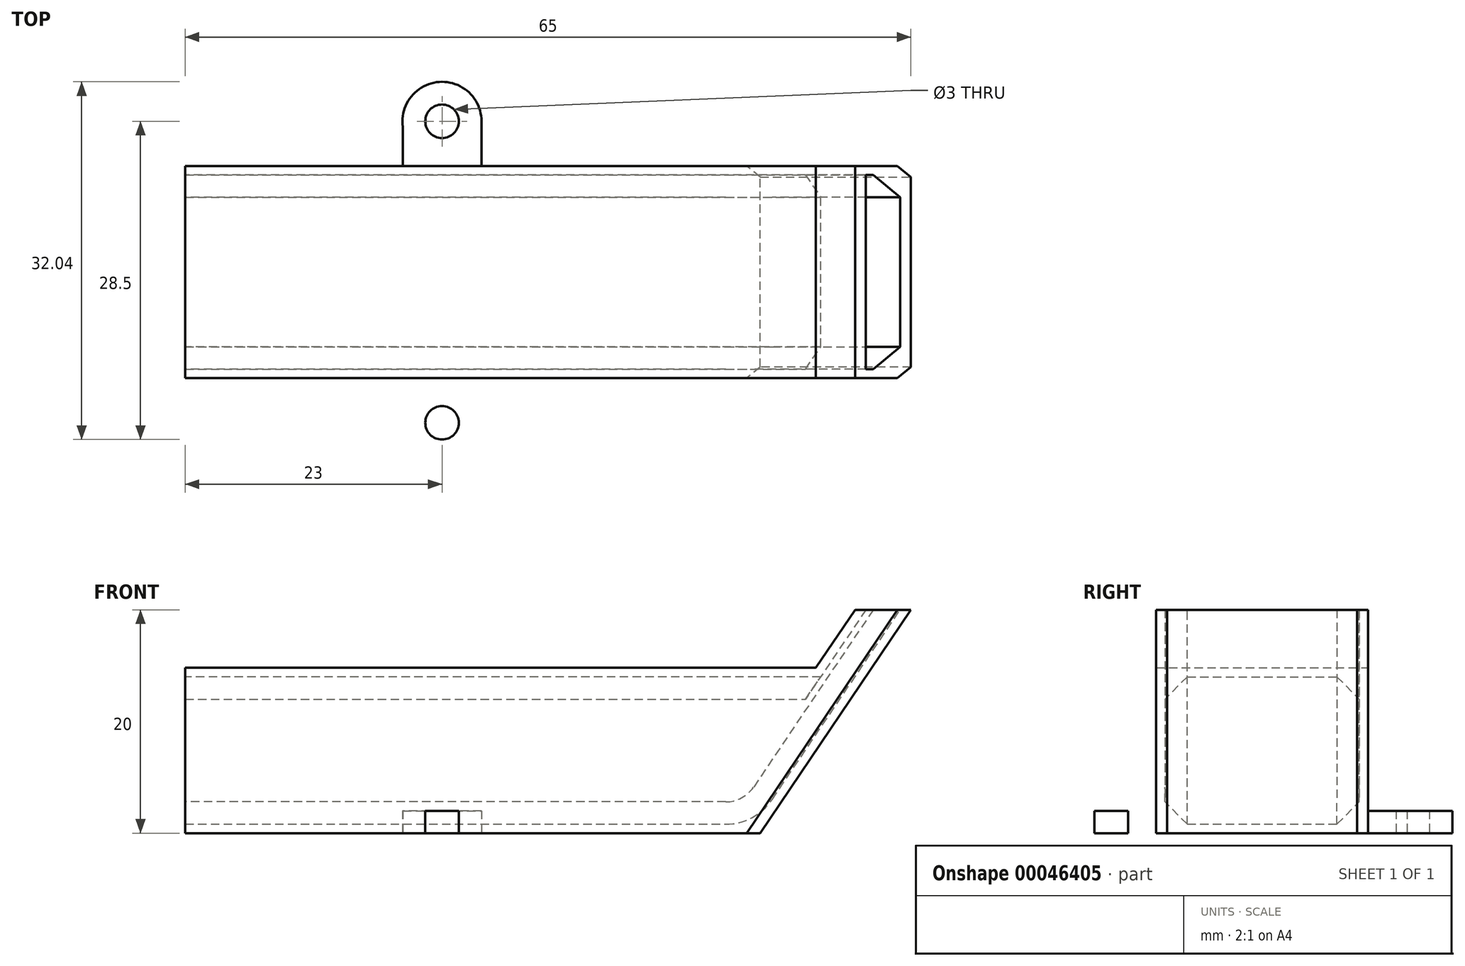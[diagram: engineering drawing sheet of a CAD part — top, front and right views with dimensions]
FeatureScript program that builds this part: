
annotation { "Feature Type Name" : "Feature", "Feature Type Description" : "" }
export const myFeature = defineFeature(function(context is Context, id is Id, definition is map)
    precondition{}
    {
        {
            var Q0;
            Q0=qCreatedBy(makeId("Top.planeOp"),FACE);
            var sketch = newSketch(context, id + "F0", { "sketchPlane" : qUnion([Q0])});
            skPoint(sketch, "E0.middle", {"position": v(0, 0) * mm});
            skLineSegment(sketch, "E1.MirrorCS", {"start": v(-24, -9.5) * mm, "end": v(-4.5, -9.5) * mm});
            skCircle(sketch, "E2.MirrorC", {"center": v(-1, -13.5) * mm, "radius": 1.5 * mm});
            skLineSegment(sketch, "E3.MirrorCS", {"start": v(-4.5, -13) * mm, "end": v(-4.5, -9.5) * mm});
            skLineSegment(sketch, "E4.MirrorCS", {"start": v(2.54, -13.5) * mm, "end": v(2.54, -9.5) * mm});
            skArc(sketch, "E5.MirrorCS", {"start": v(-4.5, -13) * mm, "mid": v(-1.25, -17.03) * mm, "end": v(2.54, -13.5) * mm});
            skLineSegment(sketch, "E6.MirrorCS", {"start": v(27.5, -9.5) * mm, "end": v(2.5, -9.5) * mm});
            skLineSegment(sketch, "E7", {"start": v(-4.5, -9.5) * mm, "end": v(2.54, -9.5) * mm});
            skLineSegment(sketch, "E8", {"start": v(27.5, -9.5) * mm, "end": v(27.5, 0) * mm});
            skLineSegment(sketch, "E9", {"start": v(-24, -9.5) * mm, "end": v(-24, 0) * mm});
            skLineSegment(sketch, "E10.MirrorCS", {"start": v(2.54, 13.5) * mm, "end": v(2.54, 9.5) * mm});
            skLineSegment(sketch, "E11.MirrorCS", {"start": v(-24, 9.5) * mm, "end": v(-24, 0) * mm});
            skLineSegment(sketch, "E12.MirrorCS", {"start": v(-4.5, 13) * mm, "end": v(-4.5, 9.5) * mm});
            skCircle(sketch, "E13.MirrorC", {"center": v(-1, 13.5) * mm, "radius": 1.5 * mm});
            skArc(sketch, "E14.MirrorCS", {"start": v(-4.5, 13) * mm, "mid": v(-1.25, 17.03) * mm, "end": v(2.54, 13.5) * mm});
            skLineSegment(sketch, "E15.MirrorCS", {"start": v(27.5, 9.5) * mm, "end": v(27.5, 0) * mm});
            skLineSegment(sketch, "E16.MirrorCS", {"start": v(-24, 9.5) * mm, "end": v(-4.5, 9.5) * mm});
            skLineSegment(sketch, "E17.MirrorCS", {"start": v(27.5, 9.5) * mm, "end": v(2.5, 9.5) * mm});
            skLineSegment(sketch, "E18.MirrorCS", {"start": v(-4.5, 9.5) * mm, "end": v(2.54, 9.5) * mm});
            skSolve(sketch);
        }
        {
            var Q0;
            Q0=qCreatedBy(makeId("Front.planeOp"),FACE);
            var sketch = newSketch(context, id + "F1", { "sketchPlane" : qUnion([Q0])});
            skLineSegment(sketch, "E19", {"start": v(27.5, 0) * mm, "end": v(-24, 0) * mm});
            skLineSegment(sketch, "E20", {"start": v(27.5, 0) * mm, "end": v(41, 20) * mm});
            skLineSegment(sketch, "E21", {"start": v(41, 20) * mm, "end": v(36, 20) * mm});
            skLineSegment(sketch, "E22", {"start": v(36, 20) * mm, "end": v(32.5, 14.8) * mm});
            skLineSegment(sketch, "E23", {"start": v(32.49, 14.8) * mm, "end": v(-24, 14.8) * mm});
            skLineSegment(sketch, "E24", {"start": v(-24, 14.8) * mm, "end": v(-24, 0) * mm});
            skSolve(sketch);
        }
        {
            var Q0;
            Q0=makeQuery(id+"F1.imprint","IMPRINT",FACE,{"disambiguationData":[TD([[makeQuery(id+"F1.imprint","IMPRINT",EDGE,{"derivedFrom":sQuery(id+"F1.wireOp",EDGE,"E19")}),-1.0]])]});
            extrude(context, id + "F2", {"entities" : qUnion([Q0]), "depth" : 19 * mm, "offsetDistance" : 25 * mm, "symmetric" : true});
        }
        {
            var Q0;
            Q0=makeQuery(id+"F2.opExtrude","SWEPT_FACE",FACE,{"disambiguationData":[OSD([sQuery(id+"F1.wireOp",EDGE,"E24")])]});
            var Q1;
            Q1=makeQuery(id+"F2.opExtrude","SWEPT_FACE",FACE,{"disambiguationData":[OSD([sQuery(id+"F1.wireOp",EDGE,"E21")])]});
            shell(context, id + "F3", {"entities" : qUnion([Q0, Q1]), "thickness" : 0.8 * mm});
        }
        {
            var Q0;
            Q0=makeQuery(id+"F3.opShell","OFFSET_EDGE",EDGE,{"disambiguationData":[OSD([sQuery(id+"F1.wireOp",EDGE,"E19"),sQuery(id+"F1.wireOp",EDGE,"E20")])]});
            fillet(context, id + "F4", {"entities" : qUnion([Q0]), "tangentPropagation" : true, "radius" : 5 * mm, "defaultsChanged" : true, "vertexSettings" : [], "allowEdgeOverflow" : false});
        }
        {
            var Q0;
            {var subQ0=sQuery(id+"F1.wireOp",EDGE,"E23");Q0=makeQuery(id+"F3.opShell","OFFSET_EDGE",EDGE,{"disambiguationData":[OSD([subQ0]),TDD([makeQuery(id+"F2.opExtrude","CAP_EDGE",EDGE,{"disambiguationData":[OSD([subQ0])],"isStart":false})])]});}
            var Q1;
            {var subQ0=sQuery(id+"F1.wireOp",EDGE,"E23");Q1=makeQuery(id+"F3.opShell","OFFSET_EDGE",EDGE,{"disambiguationData":[OSD([subQ0]),TDD([makeQuery(id+"F2.opExtrude","CAP_EDGE",EDGE,{"disambiguationData":[OSD([subQ0])],"isStart":true})])]});}
            var Q2;
            {var subQ0=sQuery(id+"F1.wireOp",EDGE,"E19");Q2=makeQuery(id+"F3.opShell","OFFSET_EDGE",EDGE,{"disambiguationData":[OSD([subQ0]),TDD([makeQuery(id+"F2.opExtrude","CAP_EDGE",EDGE,{"disambiguationData":[OSD([subQ0])],"isStart":true})])]});}
            var Q3;
            {var subQ0=sQuery(id+"F1.wireOp",EDGE,"E19");Q3=makeQuery(id+"F3.opShell","OFFSET_EDGE",EDGE,{"disambiguationData":[OSD([subQ0]),TDD([makeQuery(id+"F2.opExtrude","CAP_EDGE",EDGE,{"disambiguationData":[OSD([subQ0])],"isStart":false})])]});}
            chamfer(context, id + "F5", {"entities" : qUnion([Q0, Q1, Q2, Q3]), "width" : 2 * mm, "tangentPropagation" : true});
        }
        {
            var Q0;
            Q0=makeQuery(id+"F0.imprint","IMPRINT",FACE,{"disambiguationData":[TD([[makeQuery(id+"F0.imprint","IMPRINT",EDGE,{"derivedFrom":sQuery(id+"F0.wireOp",EDGE,"E2.MirrorC")}),1.0]])]});
            var Q1;
            {var subQ0=sQuery(id+"F0.wireOp",EDGE,"E10.MirrorCS");Q1=makeQuery(id+"F0.imprint","IMPRINT",FACE,{"disambiguationData":[TD([[makeQuery(id+"F0.imprint","IMPRINT",EDGE,{"derivedFrom":subQ0}),-1.0]])]});}
            extrude(context, id + "F6", {"entities" : qUnion([Q0, Q1]), "operationType" : NewBodyOperationType.ADD, "depth" : 2 * mm, "offsetDistance" : 25 * mm});
        }
        {
            var Q0;
            {var subQ0=sQuery(id+"F1.wireOp",EDGE,"E20");Q0=makeQuery(id+"F3.opShell","OFFSET_EDGE",EDGE,{"disambiguationData":[OSD([subQ0]),TDD([makeQuery(id+"F2.opExtrude","CAP_EDGE",EDGE,{"disambiguationData":[OSD([subQ0])],"isStart":false})])]});}
            var Q1;
            {var subQ0=sQuery(id+"F1.wireOp",EDGE,"E20");Q1=makeQuery(id+"F3.opShell","OFFSET_EDGE",EDGE,{"disambiguationData":[OSD([subQ0]),TDD([makeQuery(id+"F2.opExtrude","CAP_EDGE",EDGE,{"disambiguationData":[OSD([subQ0])],"isStart":true})])]});}
            var Q2;
            Q2=makeQuery(id+"F2.opExtrude","CAP_EDGE",EDGE,{"disambiguationData":[OSD([sQuery(id+"F1.wireOp",EDGE,"E20")])],"isStart":true});
            var Q3;
            Q3=makeQuery(id+"F2.opExtrude","CAP_EDGE",EDGE,{"disambiguationData":[OSD([sQuery(id+"F1.wireOp",EDGE,"E20")])],"isStart":false});
            chamfer(context, id + "F7", {"entities" : qUnion([Q0, Q1, Q2, Q3]), "width" : 1 * mm, "tangentPropagation" : true});
        }
    });
